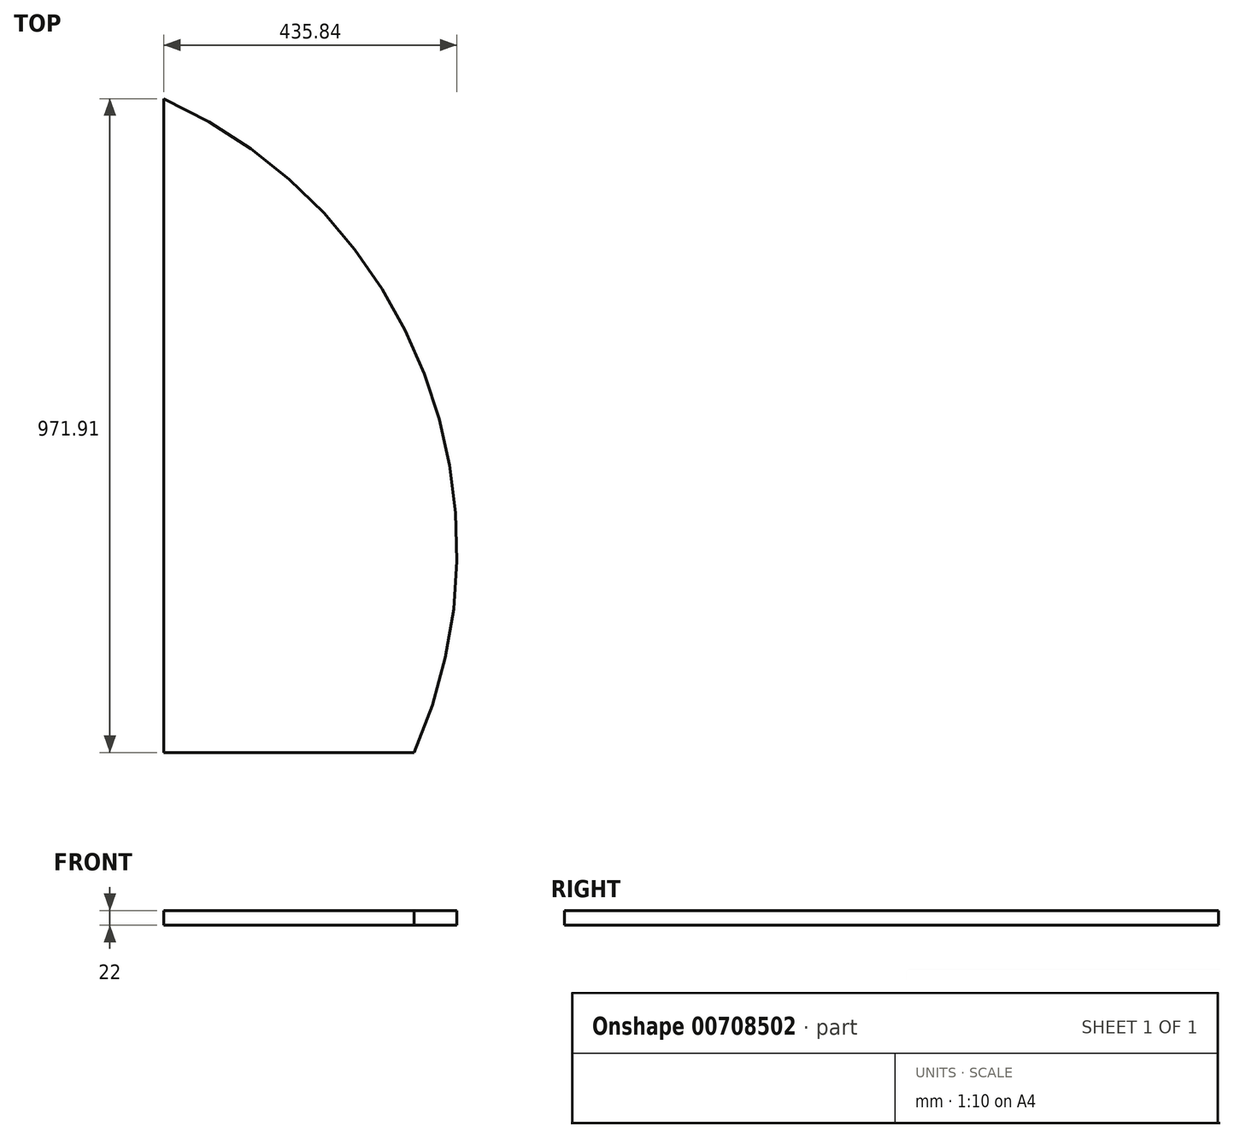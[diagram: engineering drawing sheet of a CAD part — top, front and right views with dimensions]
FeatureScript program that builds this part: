
annotation { "Feature Type Name" : "Feature", "Feature Type Description" : "" }
export const myFeature = defineFeature(function(context is Context, id is Id, definition is map)
    precondition{}
    {
        {
            var Q0;
            Q0=qCreatedBy(makeId("Top.planeOp"),FACE);
            var sketch = newSketch(context, id + "F0", { "sketchPlane" : qUnion([Q0])});
            skLineSegment(sketch, "E0.right", {"start": v(300, -300) * mm, "end": v(300, 250) * mm});
            skPoint(sketch, "E0.middle", {"position": v(0, 0) * mm});
            skPoint(sketch, "E1.end.orphan", {"position": v(-300, -300) * mm});
            skPoint(sketch, "E2.visualSharp", {"position": v(-300, 300) * mm});
            skPoint(sketch, "E3.visualSharp", {"position": v(-300, -52.1) * mm});
            skPoint(sketch, "E4.visualSharp", {"position": v(300, 300) * mm});
            skLineSegment(sketch, "E5", {"start": v(-300, -2.1) * mm, "end": v(-300, -2.1) * mm});
            skArc(sketch, "E6", {"start": v(671.9, -300) * mm, "mid": v(687.24, 262.98) * mm, "end": v(300, 671.9) * mm});
            skPoint(sketch, "E7.visualSharp", {"position": v(-300, -74.1) * mm});
            skLineSegment(sketch, "E8", {"start": v(300, -300) * mm, "end": v(671.9, -300) * mm});
            skPoint(sketch, "E9.end.orphan", {"position": v(-732.48, -70.26) * mm});
            skPoint(sketch, "E10.orphan", {"position": v(-734.26, -48.26) * mm});
            skLineSegment(sketch, "E11", {"start": v(300, 250) * mm, "end": v(300, 671.9) * mm});
            skPoint(sketch, "E2.filletArc.end.orphan", {"position": v(-300, 250) * mm});
            skSolve(sketch);
        }
        {
            var Q0;
            Q0 = qSketchRegion(id + "F0", true);
            extrude(context, id + "F1", {"entities" : qUnion([Q0]), "depth" : 22 * mm, "offsetDistance" : 25 * mm});
        }
    });
